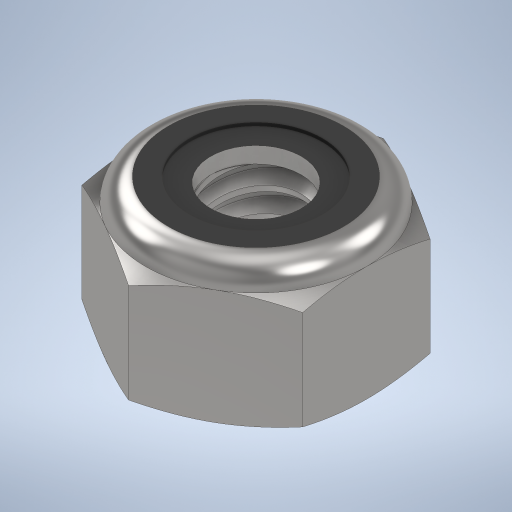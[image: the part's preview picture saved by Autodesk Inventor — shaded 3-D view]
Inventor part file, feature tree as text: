
AUTODESK INVENTOR PART (.ipt)
format: ipt  version: 2024 (Build 280153000, 153)  size: 406,528 bytes
history: native  units: in
note: dims shown in document units (in); Inventor stores cm internally (conversion verified against a paired STEP export)
features: other x1, revolve x1
ambient origin geometry x8: Origin, YZ Plane, XZ Plane, XY Plane, X Axis, Y Axis, Z Axis, Center Point
bodies: Solid1 (feature_tree), Solid2 (feature_tree)
feature tree (2):
  other  "Cut-Revolve4"
  revolve  "Revolve2"  [1 undecoded]
note: 1 required parameter value undecoded (feature->parameter linkage not recoverable at this tier; creation-order binding heuristic only, values carry confidence <= 0.55)
